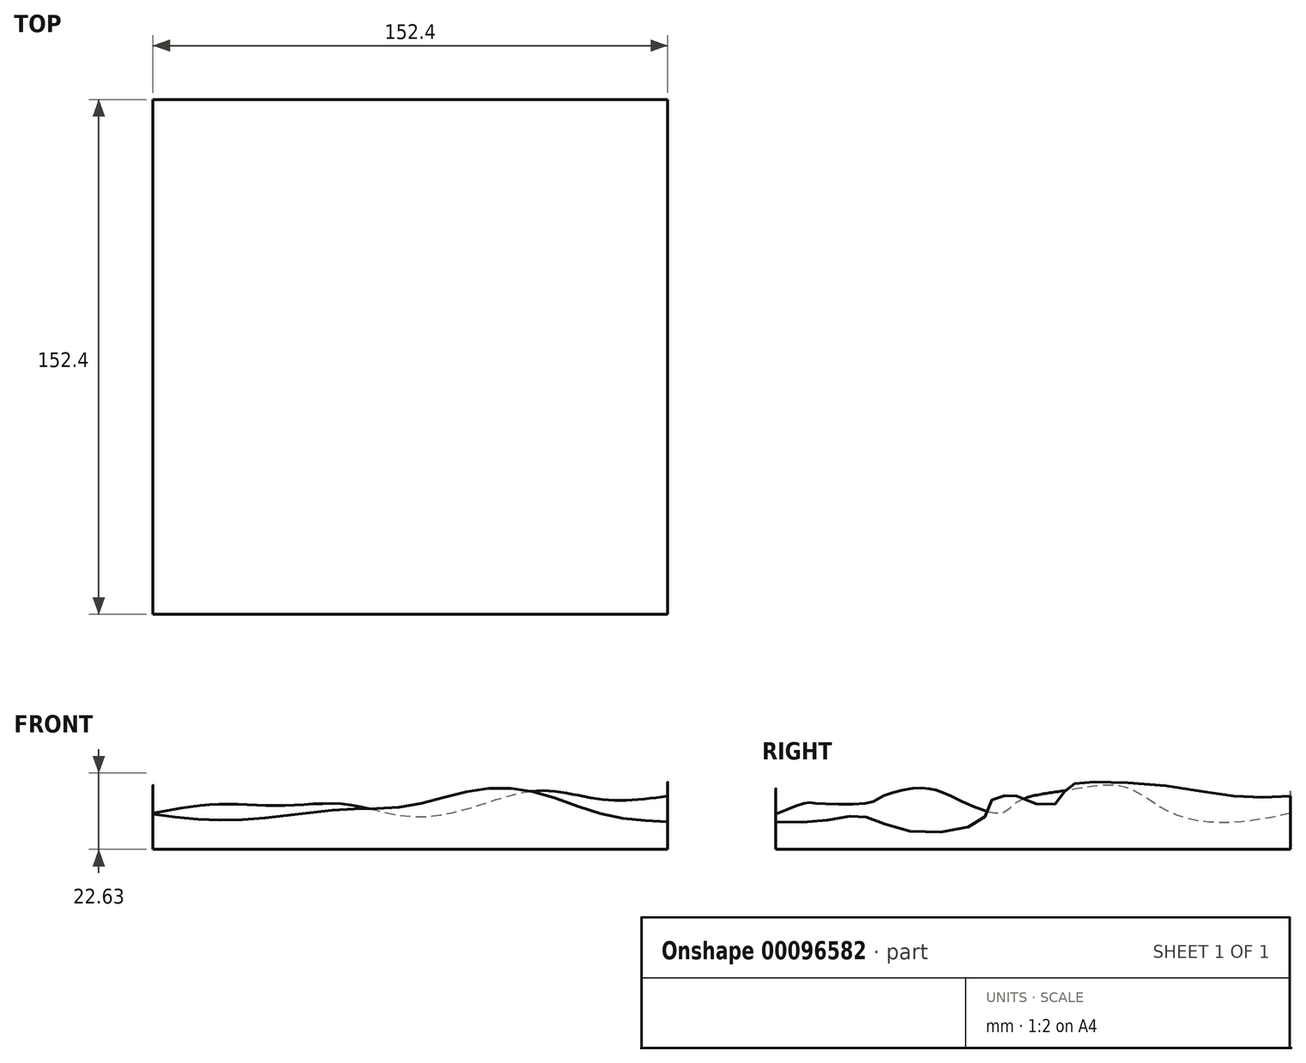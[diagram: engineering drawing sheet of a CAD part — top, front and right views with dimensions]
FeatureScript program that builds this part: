
annotation { "Feature Type Name" : "Feature", "Feature Type Description" : "" }
export const myFeature = defineFeature(function(context is Context, id is Id, definition is map)
    precondition{}
    {
        {
            var Q0;
            Q0=qCreatedBy(makeId("Top.planeOp"),FACE);
            var sketch = newSketch(context, id + "F0", { "sketchPlane" : qUnion([Q0])});
            skLineSegment(sketch, "E0.bottom", {"start": v(76.2, 76.2) * mm, "end": v(-76.2, 76.2) * mm});
            skLineSegment(sketch, "E0.top", {"start": v(76.2, -76.2) * mm, "end": v(-76.2, -76.2) * mm});
            skLineSegment(sketch, "E0.left", {"start": v(76.2, 76.2) * mm, "end": v(76.2, -76.2) * mm});
            skLineSegment(sketch, "E0.right", {"start": v(-76.2, 76.2) * mm, "end": v(-76.2, -76.2) * mm});
            skPoint(sketch, "E0.middle", {"position": v(0, 0) * mm});
            skSolve(sketch);
        }
        {
            var Q0;
            Q0=qCreatedBy(makeId("Right.planeOp"),FACE);
            cPlane(context, id + "F1", {"entities" : qUnion([Q0]), "cplaneType" : CPlaneType.OFFSET, "offset" : 76.2 * mm, "width" : 150 * mm, "height" : 150 * mm});
        }
        {
            var Q0;
            Q0=qCreatedBy(makeId("Right.planeOp"),FACE);
            cPlane(context, id + "F2", {"entities" : qUnion([Q0]), "cplaneType" : CPlaneType.OFFSET, "offset" : 76.2 * mm, "oppositeDirection" : true, "width" : 150 * mm, "height" : 150 * mm});
        }
        {
            var Q0;
            Q0=qCreatedBy(id+"F2.planeOp",FACE);
            var Q1;
            Q1=qCreatedBy(makeId("Right.planeOp"),FACE);
            cPlane(context, id + "F3", {"entities" : qUnion([Q0, Q1]), "cplaneType" : CPlaneType.MID_PLANE, "offset" : 150 * mm, "width" : 150 * mm, "height" : 150 * mm});
        }
        {
            var Q0;
            Q0=qCreatedBy(makeId("Right.planeOp"),FACE);
            var Q1;
            Q1=qCreatedBy(id+"F1.planeOp",FACE);
            cPlane(context, id + "F4", {"entities" : qUnion([Q0, Q1]), "cplaneType" : CPlaneType.MID_PLANE, "offset" : 150 * mm, "width" : 150 * mm, "height" : 150 * mm});
        }
        {
            var Q0;
            Q0=qCreatedBy(id+"F2.planeOp",FACE);
            var Q1;
            Q1=qCreatedBy(id+"F3.planeOp",FACE);
            cPlane(context, id + "F5", {"entities" : qUnion([Q0, Q1]), "cplaneType" : CPlaneType.MID_PLANE, "offset" : 150 * mm, "width" : 150 * mm, "height" : 150 * mm});
        }
        {
            var Q0;
            Q0=qCreatedBy(id+"F3.planeOp",FACE);
            var Q1;
            Q1=qCreatedBy(makeId("Right.planeOp"),FACE);
            cPlane(context, id + "F6", {"entities" : qUnion([Q0, Q1]), "cplaneType" : CPlaneType.MID_PLANE, "offset" : 150 * mm, "width" : 150 * mm, "height" : 150 * mm});
        }
        {
            var Q0;
            Q0=qCreatedBy(makeId("Right.planeOp"),FACE);
            var Q1;
            Q1=qCreatedBy(id+"F4.planeOp",FACE);
            cPlane(context, id + "F7", {"entities" : qUnion([Q0, Q1]), "cplaneType" : CPlaneType.MID_PLANE, "offset" : 150 * mm, "width" : 150 * mm, "height" : 150 * mm});
        }
        {
            var Q0;
            Q0=qCreatedBy(id+"F4.planeOp",FACE);
            var Q1;
            Q1=qCreatedBy(id+"F1.planeOp",FACE);
            cPlane(context, id + "F8", {"entities" : qUnion([Q0, Q1]), "cplaneType" : CPlaneType.MID_PLANE, "offset" : 150 * mm, "width" : 150 * mm, "height" : 150 * mm});
        }
        {
            var Q0;
            Q0=qCreatedBy(id+"F2.planeOp",FACE);
            var sketch = newSketch(context, id + "F9", { "sketchPlane" : qUnion([Q0])});
            skLineSegment(sketch, "E1", {"start": v(76.2, 0) * mm, "end": v(76.2, 10.7) * mm});
            skLineSegment(sketch, "E2", {"start": v(76.2, 0) * mm, "end": v(-76.2, 0) * mm});
            skLineSegment(sketch, "E3", {"start": v(-76.2, 0) * mm, "end": v(-76.2, 10.49) * mm});
            skFitSpline(sketch, "E4", {"points": [v(76.2, 10.7) * mm, v(59.96, 8.05) * mm, v(41.13, 10.7) * mm, v(27.45, 18.34) * mm, v(11.2, 17.66) * mm, v(-4.52, 14.14) * mm, v(-9.8, 10.7) * mm, v(-24.3, 15.77) * mm, v(-29.85, 17.8) * mm, v(-36.9, 17.93) * mm, v(-45.29, 15.36) * mm, v(-48.54, 13.87) * mm, v(-63.71, 13.6) * mm, v(-67.37, 13.73) * mm, v(-76.2, 10.49) * mm], "startDerivative": vector(-175.86, -38.59) * mm, "endDerivative": vector(-153.26, -64.55) * mm});
            skSolve(sketch);
        }
        {
            var Q0;
            Q0=qCreatedBy(id+"F5.planeOp",FACE);
            var sketch = newSketch(context, id + "F10", { "sketchPlane" : qUnion([Q0])});
            skLineSegment(sketch, "E5.1", {"start": v(76.2, 0) * mm, "end": v(-76.2, 0) * mm});
            skLineSegment(sketch, "E6", {"start": v(76.2, 0) * mm, "end": v(76.2, 13.36) * mm});
            skLineSegment(sketch, "E7", {"start": v(-76.2, 0) * mm, "end": v(-76.2, 8.64) * mm});
            skFitSpline(sketch, "E8", {"points": [v(76.2, 13.36) * mm, v(67.59, 11.37) * mm, v(58.25, 8.73) * mm, v(50.13, 10.35) * mm, v(39.98, 13.36) * mm, v(29.23, 16.44) * mm, v(12.38, 15.83) * mm, v(3.86, 13.36) * mm, v(-4.06, 11.16) * mm, v(-11.57, 8.12) * mm, v(-21.51, 11.57) * mm, v(-28, 13.36) * mm, v(-38.16, 13.36) * mm, v(-46.68, 11.16) * mm, v(-57.03, 11.77) * mm, v(-70.43, 10.76) * mm, v(-76.2, 8.64) * mm], "startDerivative": vector(-141.74, -26.31) * mm, "endDerivative": vector(-100.24, -46.38) * mm});
            skSolve(sketch);
        }
        {
            var Q0;
            Q0=qCreatedBy(id+"F3.planeOp",FACE);
            var sketch = newSketch(context, id + "F11", { "sketchPlane" : qUnion([Q0])});
            skLineSegment(sketch, "E9.0", {"start": v(76.2, 0) * mm, "end": v(-76.2, 0) * mm});
            skLineSegment(sketch, "E10", {"start": v(76.2, 0) * mm, "end": v(76.2, 12.96) * mm});
            skLineSegment(sketch, "E11", {"start": v(-76.2, 0) * mm, "end": v(-76.2, 9.86) * mm});
            skFitSpline(sketch, "E12", {"points": [v(76.2, 12.96) * mm, v(67.38, 9.74) * mm, v(50.74, 8.73) * mm, v(37.75, 12.96) * mm, v(25.98, 14.61) * mm, v(7.5, 12.96) * mm, v(-2.44, 8.32) * mm, v(-7.1, 6.3) * mm, v(-16.03, 9.95) * mm, v(-27.6, 15.83) * mm, v(-38.16, 19.08) * mm, v(-53.18, 19.48) * mm, v(-63.12, 19.08) * mm, v(-67.59, 16.64) * mm, v(-70.82, 11.6) * mm, v(-76.2, 9.86) * mm], "startDerivative": vector(-124.1, -54.9) * mm, "endDerivative": vector(-122.97, -15.69) * mm});
            skSolve(sketch);
        }
        {
            var Q0;
            Q0=qCreatedBy(id+"F6.planeOp",FACE);
            var sketch = newSketch(context, id + "F12", { "sketchPlane" : qUnion([Q0])});
            skLineSegment(sketch, "E13.0", {"start": v(76.2, 0) * mm, "end": v(-76.2, 0) * mm});
            skLineSegment(sketch, "E14", {"start": v(-76.2, 0) * mm, "end": v(-76.2, 11.86) * mm});
            skLineSegment(sketch, "E15", {"start": v(76.2, 0) * mm, "end": v(76.2, 13.34) * mm});
            skFitSpline(sketch, "E16", {"points": [v(76.2, 13.34) * mm, v(68.65, 11.1) * mm, v(56.95, 10.55) * mm, v(46.05, 13.34) * mm, v(36.92, 18.08) * mm, v(24.22, 18.71) * mm, v(13.28, 13.34) * mm, v(4.27, 9) * mm, v(-8.96, 11.17) * mm, v(-22.33, 16.89) * mm, v(-27.75, 20.39) * mm, v(-39.16, 20.63) * mm, v(-43.28, 18.74) * mm, v(-50.46, 19.6) * mm, v(-54.37, 20.18) * mm, v(-63.62, 13.34) * mm, v(-76.2, 11.86) * mm], "startDerivative": vector(-126, -45.35) * mm, "endDerivative": vector(-184.02, 11.67) * mm});
            skSolve(sketch);
        }
        {
            var Q0;
            Q0=qCreatedBy(makeId("Right.planeOp"),FACE);
            var sketch = newSketch(context, id + "F13", { "sketchPlane" : qUnion([Q0])});
            skLineSegment(sketch, "E17.0", {"start": v(76.2, 0) * mm, "end": v(-76.2, 0) * mm});
            skLineSegment(sketch, "E18", {"start": v(76.2, 0) * mm, "end": v(76.2, 9.76) * mm});
            skLineSegment(sketch, "E19", {"start": v(-76.2, 0) * mm, "end": v(-76.2, 12.9) * mm});
            skFitSpline(sketch, "E20", {"points": [v(-76.2, 12.9) * mm, v(-68.9, 15.37) * mm, v(-63.79, 18.3) * mm, v(-55.23, 19.35) * mm, v(-49.29, 15.21) * mm, v(-42.56, 18.9) * mm, v(-34.09, 20.83) * mm, v(-18.2, 18.2) * mm, v(-5.54, 12.9) * mm, v(7.35, 11.43) * mm, v(14.87, 14.6) * mm, v(24.34, 17.44) * mm, v(42.07, 17.98) * mm, v(59.6, 11.05) * mm, v(76.2, 9.76) * mm], "startDerivative": vector(131.17, 35.62) * mm, "endDerivative": vector(211.48, -49.38) * mm});
            skSolve(sketch);
        }
        {
            var Q0;
            Q0=qCreatedBy(id+"F7.planeOp",FACE);
            var sketch = newSketch(context, id + "F14", { "sketchPlane" : qUnion([Q0])});
            skLineSegment(sketch, "E21.0", {"start": v(76.2, 0) * mm, "end": v(-76.2, 0) * mm});
            skLineSegment(sketch, "E22", {"start": v(-76.2, 0) * mm, "end": v(-76.2, 17.57) * mm});
            skLineSegment(sketch, "E23", {"start": v(76.2, 0) * mm, "end": v(76.2, 12.67) * mm});
            skFitSpline(sketch, "E24", {"points": [v(76.2, 12.67) * mm, v(62.72, 14.68) * mm, v(49.37, 17.53) * mm, v(36.08, 21.03) * mm, v(17.1, 19.47) * mm, v(6.8, 16.4) * mm, v(-9.75, 18.5) * mm, v(-26.5, 19.71) * mm, v(-40.24, 12.67) * mm, v(-48.44, 10.3) * mm, v(-56.06, 12.67) * mm, v(-63.76, 15.64) * mm, v(-76.2, 17.57) * mm], "startDerivative": vector(-156.64, 22.08) * mm, "endDerivative": vector(-165.53, 0.73) * mm});
            skSolve(sketch);
        }
        {
            var Q0;
            Q0=qCreatedBy(id+"F4.planeOp",FACE);
            var sketch = newSketch(context, id + "F15", { "sketchPlane" : qUnion([Q0])});
            skLineSegment(sketch, "E25.0", {"start": v(76.2, 0) * mm, "end": v(-76.2, 0) * mm});
            skLineSegment(sketch, "E26", {"start": v(76.2, 0) * mm, "end": v(76.2, 17.4) * mm});
            skLineSegment(sketch, "E27", {"start": v(-76.2, 0) * mm, "end": v(-76.2, 16.67) * mm});
            skFitSpline(sketch, "E28", {"points": [v(-76.2, 16.67) * mm, v(-65.51, 16.67) * mm, v(-52.48, 13) * mm, v(-46.57, 8.68) * mm, v(-36.27, 4.56) * mm, v(-23.07, 4.49) * mm, v(-15.14, 9.97) * mm, v(-9.63, 16.67) * mm, v(0, 16.67) * mm, v(14.26, 16.67) * mm, v(37.26, 21.13) * mm, v(76.2, 17.4) * mm], "startDerivative": vector(127.02, 12.24) * mm, "endDerivative": vector(249.83, -32.98) * mm});
            skSolve(sketch);
        }
        {
            var Q0;
            Q0=qCreatedBy(id+"F8.planeOp",FACE);
            var sketch = newSketch(context, id + "F16", { "sketchPlane" : qUnion([Q0])});
            skLineSegment(sketch, "E29.0", {"start": v(76.2, 0) * mm, "end": v(-76.2, 0) * mm});
            skLineSegment(sketch, "E30", {"start": v(76.2, 0) * mm, "end": v(76.2, 14.8) * mm});
            skLineSegment(sketch, "E31", {"start": v(-76.2, 0) * mm, "end": v(-76.2, 10.39) * mm});
            skFitSpline(sketch, "E32", {"points": [v(76.2, 14.8) * mm, v(56.33, 20.25) * mm, v(35.66, 22.21) * mm, v(29.8, 21.09) * mm, v(18.27, 21.15) * mm, v(14.18, 20.82) * mm, v(6.28, 14.8) * mm, v(-3.47, 14.8) * mm, v(-10.38, 14.8) * mm, v(-13.77, 9.08) * mm, v(-23.93, 4.82) * mm, v(-39.06, 5.84) * mm, v(-45.27, 10.64) * mm, v(-51.77, 14.58) * mm, v(-57.84, 14.8) * mm, v(-66.5, 11.93) * mm, v(-76.2, 10.39) * mm], "startDerivative": vector(-207.9, 20.47) * mm, "endDerivative": vector(-128.58, -16.2) * mm});
            skSolve(sketch);
        }
        {
            var Q0;
            Q0=qCreatedBy(id+"F1.planeOp",FACE);
            var sketch = newSketch(context, id + "F17", { "sketchPlane" : qUnion([Q0])});
            skLineSegment(sketch, "E33.0", {"start": v(76.2, 0) * mm, "end": v(-76.2, 0) * mm});
            skLineSegment(sketch, "E34", {"start": v(-76.2, 0) * mm, "end": v(-76.2, 8.18) * mm});
            skLineSegment(sketch, "E35", {"start": v(76.2, 0) * mm, "end": v(76.2, 15.77) * mm});
            skFitSpline(sketch, "E36", {"points": [v(76.2, 15.77) * mm, v(60.21, 15.77) * mm, v(36.76, 19.15) * mm, v(14.76, 19.83) * mm, v(11.08, 18.9) * mm, v(8.39, 15.77) * mm, v(4.44, 12.7) * mm, v(-4.47, 15.77) * mm, v(-6.79, 15.77) * mm, v(-11.34, 15.77) * mm, v(-13.59, 10.82) * mm, v(-19.53, 6.5) * mm, v(-36.9, 5.42) * mm, v(-47.8, 9.04) * mm, v(-52.84, 9.94) * mm, v(-62.56, 8.4) * mm, v(-76.2, 8.18) * mm], "startDerivative": vector(-185.87, -9.58) * mm, "endDerivative": vector(-181.97, 6) * mm});
            skSolve(sketch);
        }
        {
            var Q0;
            Q0=makeQuery(id+"F9.imprint","IMPRINT",FACE,{"disambiguationData":[TD([[makeQuery(id+"F9.imprint","IMPRINT",EDGE,{"derivedFrom":sQuery(id+"F9.wireOp",EDGE,"E1")}),1.0]])]});
            var Q1;
            Q1=makeQuery(id+"F10.imprint","IMPRINT",FACE,{"disambiguationData":[TD([[makeQuery(id+"F10.imprint","IMPRINT",EDGE,{"derivedFrom":sQuery(id+"F10.wireOp",EDGE,"E5.1")}),-1.0]])]});
            var Q2;
            Q2=makeQuery(id+"F11.imprint","IMPRINT",FACE,{"disambiguationData":[TD([[makeQuery(id+"F11.imprint","IMPRINT",EDGE,{"derivedFrom":sQuery(id+"F11.wireOp",EDGE,"E9.0")}),-1.0]])]});
            var Q3;
            Q3=makeQuery(id+"F12.imprint","IMPRINT",FACE,{"disambiguationData":[TD([[makeQuery(id+"F12.imprint","IMPRINT",EDGE,{"derivedFrom":sQuery(id+"F12.wireOp",EDGE,"E13.0")}),-1.0]])]});
            var Q4;
            Q4=makeQuery(id+"F13.imprint","IMPRINT",FACE,{"disambiguationData":[TD([[makeQuery(id+"F13.imprint","IMPRINT",EDGE,{"derivedFrom":sQuery(id+"F13.wireOp",EDGE,"E17.0")}),-1.0]])]});
            var Q5;
            Q5=makeQuery(id+"F14.imprint","IMPRINT",FACE,{"disambiguationData":[TD([[makeQuery(id+"F14.imprint","IMPRINT",EDGE,{"derivedFrom":sQuery(id+"F14.wireOp",EDGE,"E21.0")}),-1.0]])]});
            var Q6;
            Q6=makeQuery(id+"F15.imprint","IMPRINT",FACE,{"disambiguationData":[TD([[makeQuery(id+"F15.imprint","IMPRINT",EDGE,{"derivedFrom":sQuery(id+"F15.wireOp",EDGE,"E25.0")}),-1.0]])]});
            var Q7;
            Q7=makeQuery(id+"F16.imprint","IMPRINT",FACE,{"disambiguationData":[TD([[makeQuery(id+"F16.imprint","IMPRINT",EDGE,{"derivedFrom":sQuery(id+"F16.wireOp",EDGE,"E29.0")}),-1.0]])]});
            var Q8;
            Q8=makeQuery(id+"F17.imprint","IMPRINT",FACE,{"disambiguationData":[TD([[makeQuery(id+"F17.imprint","IMPRINT",EDGE,{"derivedFrom":sQuery(id+"F17.wireOp",EDGE,"E33.0")}),-1.0]])]});
            loft(context, id + "F18", {"sheetProfilesArray" : [{ "sheetProfileEntities" : qUnion([Q0]) }, { "sheetProfileEntities" : qUnion([Q1]) }, { "sheetProfileEntities" : qUnion([Q2]) }, { "sheetProfileEntities" : qUnion([Q3]) }, { "sheetProfileEntities" : qUnion([Q4]) }, { "sheetProfileEntities" : qUnion([Q5]) }, { "sheetProfileEntities" : qUnion([Q6]) }, { "sheetProfileEntities" : qUnion([Q7]) }, { "sheetProfileEntities" : qUnion([Q8]) }]});
        }
        {
            var Q0;
            Q0=makeQuery(id+"F0.imprint","IMPRINT",FACE,{"disambiguationData":[TD([[makeQuery(id+"F0.imprint","IMPRINT",EDGE,{"derivedFrom":sQuery(id+"F0.wireOp",EDGE,"E0.bottom")}),1.0]])]});
            cPlane(context, id + "F19", {"entities" : qUnion([Q0]), "cplaneType" : CPlaneType.OFFSET, "offset" : 3.17 * mm, "width" : 150 * mm, "height" : 150 * mm});
        }
        {
            var Q0;
            Q0=qCreatedBy(id+"F19.planeOp",FACE);
            cPlane(context, id + "F20", {"entities" : qUnion([Q0]), "cplaneType" : CPlaneType.OFFSET, "offset" : 3.17 * mm, "width" : 150 * mm, "height" : 150 * mm});
        }
        {
            var Q0;
            Q0=qCreatedBy(id+"F20.planeOp",FACE);
            cPlane(context, id + "F21", {"entities" : qUnion([Q0]), "cplaneType" : CPlaneType.OFFSET, "offset" : 3.17 * mm, "width" : 150 * mm, "height" : 150 * mm});
        }
        {
            var Q0;
            Q0=qCreatedBy(id+"F21.planeOp",FACE);
            cPlane(context, id + "F22", {"entities" : qUnion([Q0]), "cplaneType" : CPlaneType.OFFSET, "offset" : 3.17 * mm, "width" : 150 * mm, "height" : 150 * mm});
        }
        {
            var Q0;
            Q0=qCreatedBy(id+"F22.planeOp",FACE);
            cPlane(context, id + "F23", {"entities" : qUnion([Q0]), "cplaneType" : CPlaneType.OFFSET, "offset" : 3.17 * mm, "width" : 150 * mm, "height" : 150 * mm});
        }
        {
            var Q0;
            Q0=qCreatedBy(id+"F23.planeOp",FACE);
            cPlane(context, id + "F24", {"entities" : qUnion([Q0]), "cplaneType" : CPlaneType.OFFSET, "offset" : 3.17 * mm, "width" : 150 * mm, "height" : 150 * mm});
        }
        {
            var Q0;
            Q0=qCreatedBy(id+"F24.planeOp",FACE);
            cPlane(context, id + "F25", {"entities" : qUnion([Q0]), "cplaneType" : CPlaneType.OFFSET, "offset" : 3.17 * mm, "width" : 150 * mm, "height" : 150 * mm});
        }
    });
